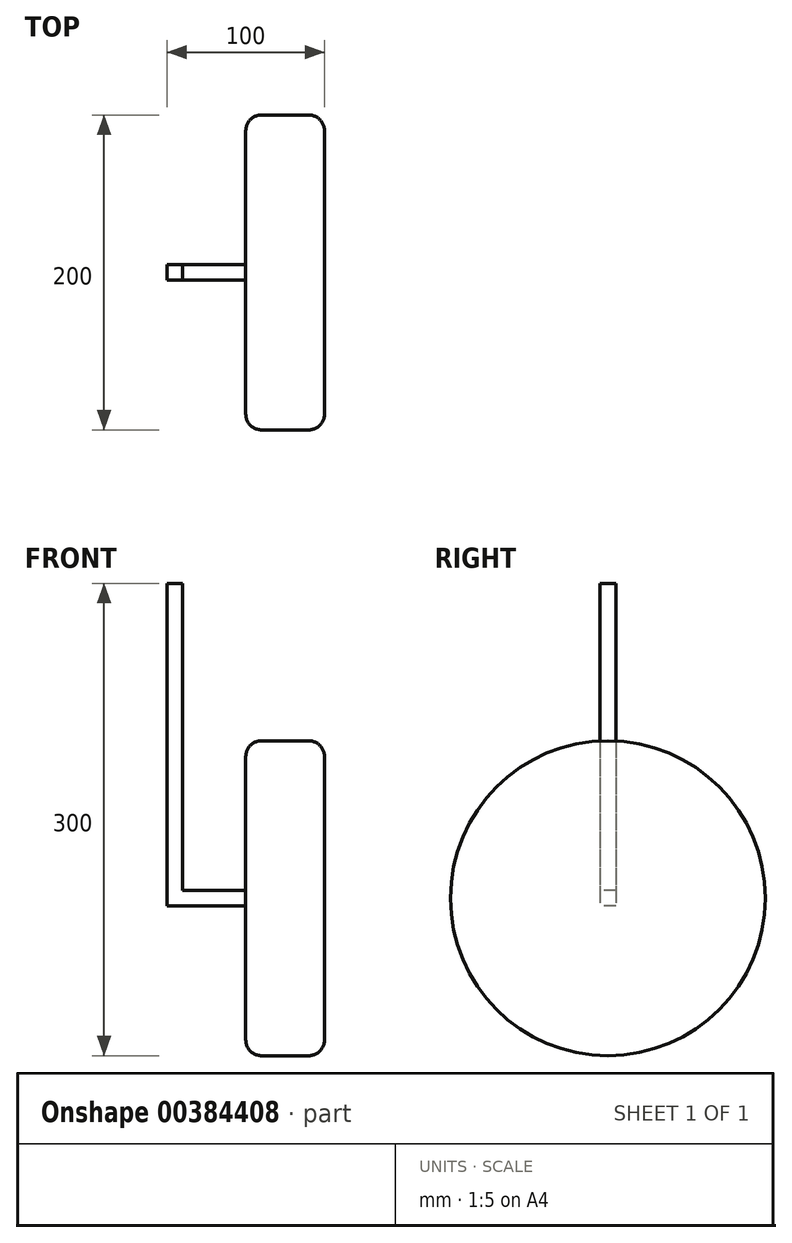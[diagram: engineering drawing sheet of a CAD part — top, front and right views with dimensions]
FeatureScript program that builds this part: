
annotation { "Feature Type Name" : "Feature", "Feature Type Description" : "" }
export const myFeature = defineFeature(function(context is Context, id is Id, definition is map)
    precondition{}
    {
        {
            var Q0;
            Q0=qCreatedBy(makeId("Right.planeOp"),FACE);
            var sketch = newSketch(context, id + "F0", { "sketchPlane" : qUnion([Q0])});
            skCircle(sketch, "E0", {"center": v(0, 0) * mm, "radius": 100 * mm});
            skSolve(sketch);
        }
        {
            var Q0;
            Q0=makeQuery(id+"F0.imprint","IMPRINT",FACE,{"disambiguationData":[TD([[makeQuery(id+"F0.imprint","IMPRINT",EDGE,{"derivedFrom":sQuery(id+"F0.wireOp",EDGE,"E0")}),1.0]])]});
            extrude(context, id + "F1", {"entities" : qUnion([Q0]), "depth" : 50 * mm});
        }
        {
            var Q0;
            Q0=makeQuery(id+"F1.opExtrude","CAP_EDGE",EDGE,{"disambiguationData":[OSD([sQuery(id+"F0.wireOp",EDGE,"E0")])],"isStart":false});
            var Q1;
            Q1=makeQuery(id+"F1.opExtrude","CAP_EDGE",EDGE,{"disambiguationData":[OSD([sQuery(id+"F0.wireOp",EDGE,"E0")])],"isStart":true});
            fillet(context, id + "F2", {"entities" : qUnion([Q0, Q1]), "radius" : 10 * mm, "tangentPropagation" : true, "allowEdgeOverflow" : false});
        }
        {
            var Q0;
            Q0=makeQuery(id+"F1.opExtrude","CAP_FACE",FACE,{"disambiguationData":[OSD([sQuery(id+"F0.wireOp",EDGE,"E0")])],"isStart":true});
            var sketch = newSketch(context, id + "F3", { "sketchPlane" : qUnion([Q0])});
            skLineSegment(sketch, "E1.bottom", {"start": v(-5, 5) * mm, "end": v(5, 5) * mm});
            skLineSegment(sketch, "E1.top", {"start": v(-5, -5) * mm, "end": v(5, -5) * mm});
            skLineSegment(sketch, "E1.left", {"start": v(-5, 5) * mm, "end": v(-5, -5) * mm});
            skLineSegment(sketch, "E1.right", {"start": v(5, 5) * mm, "end": v(5, -5) * mm});
            skPoint(sketch, "E1.middle", {"position": v(0, 0) * mm});
            skSolve(sketch);
        }
        {
            var Q0;
            Q0=makeQuery(id+"F3.imprint","IMPRINT",FACE,{"disambiguationData":[TD([[makeQuery(id+"F3.imprint","IMPRINT",EDGE,{"derivedFrom":sQuery(id+"F3.wireOp",EDGE,"E1.bottom")}),-1.0]])]});
            extrude(context, id + "F4", {"entities" : qUnion([Q0]), "operationType" : NewBodyOperationType.ADD, "depth" : 50 * mm});
        }
        {
            var Q0;
            Q0=makeQuery(id+"F4.opExtrude","SWEPT_FACE",FACE,{"disambiguationData":[OSD([sQuery(id+"F3.wireOp",EDGE,"E1.bottom")])]});
            var sketch = newSketch(context, id + "F5", { "sketchPlane" : qUnion([Q0])});
            skLineSegment(sketch, "E2.bottom", {"start": v(-50, 5) * mm, "end": v(-40, 5) * mm});
            skLineSegment(sketch, "E2.top", {"start": v(-50, -5) * mm, "end": v(-40, -5) * mm});
            skLineSegment(sketch, "E2.left", {"start": v(-50, 5) * mm, "end": v(-50, -5) * mm});
            skLineSegment(sketch, "E2.right", {"start": v(-40, 5) * mm, "end": v(-40, -5) * mm});
            skSolve(sketch);
        }
        {
            var Q0;
            Q0=makeQuery(id+"F5.imprint","IMPRINT",FACE,{"disambiguationData":[TD([[makeQuery(id+"F5.imprint","IMPRINT",EDGE,{"derivedFrom":sQuery(id+"F5.wireOp",EDGE,"E2.bottom")}),-1.0]])]});
            extrude(context, id + "F6", {"entities" : qUnion([Q0]), "operationType" : NewBodyOperationType.ADD, "depth" : 195 * mm});
        }
    });
